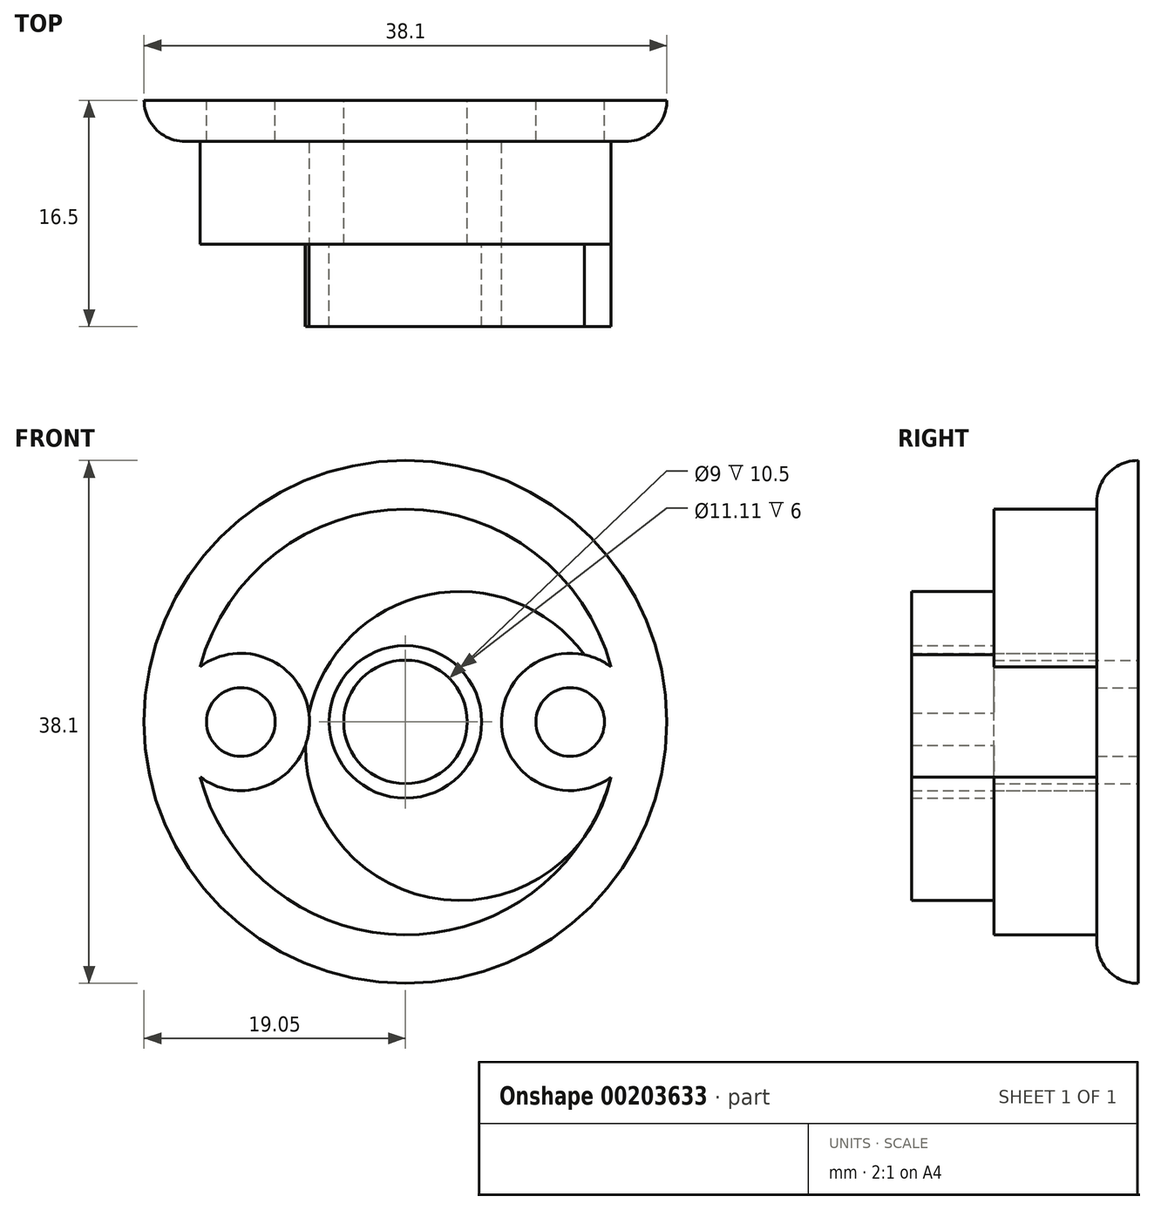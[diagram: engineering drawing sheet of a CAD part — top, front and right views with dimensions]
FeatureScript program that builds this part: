
annotation { "Feature Type Name" : "Feature", "Feature Type Description" : "" }
export const myFeature = defineFeature(function(context is Context, id is Id, definition is map)
    precondition{}
    {
        {
            var Q0;
            Q0=qCreatedBy(makeId("Front.planeOp"),FACE);
            var sketch = newSketch(context, id + "F0", { "sketchPlane" : qUnion([Q0])});
            skCircle(sketch, "E0", {"center": v(0, 0) * mm, "radius": 19.05 * mm});
            skCircle(sketch, "E1", {"center": v(0, 0) * mm, "radius": 4.5 * mm});
            skCircle(sketch, "E2", {"center": v(-12, 0) * mm, "radius": 2.5 * mm});
            skCircle(sketch, "E3.MirrorC", {"center": v(12, 0) * mm, "radius": 2.5 * mm});
            skSolve(sketch);
        }
        {
            var Q0;
            Q0 = qSketchRegion(id + "F0", true);
            extrude(context, id + "F1", {"entities" : qUnion([Q0]), "depth" : 3 * mm});
        }
        {
            var Q0;
            Q0=makeQuery(id+"F1.opExtrude","CAP_EDGE",EDGE,{"disambiguationData":[OSD([sQuery(id+"F0.wireOp",EDGE,"E0")])],"isStart":false});
            fillet(context, id + "F2", {"entities" : qUnion([Q0]), "radius" : 3 * mm, "tangentPropagation" : true, "allowEdgeOverflow" : false});
        }
        {
            var Q0;
            Q0=makeQuery(id+"F1.opExtrude","CAP_FACE",FACE,{"disambiguationData":[OSD([sQuery(id+"F0.wireOp",EDGE,"E0"),sQuery(id+"F0.wireOp",EDGE,"E1"),sQuery(id+"F0.wireOp",EDGE,"E2"),sQuery(id+"F0.wireOp",EDGE,"E3.MirrorC")])],"isStart":false});
            var sketch = newSketch(context, id + "F3", { "sketchPlane" : qUnion([Q0])});
            skCircle(sketch, "E4", {"center": v(0, 0) * mm, "radius": 15.5 * mm});
            skCircle(sketch, "E5.0", {"center": v(0, 0) * mm, "radius": 4.5 * mm});
            skCircle(sketch, "E6", {"center": v(-12, 0) * mm, "radius": 5 * mm});
            skCircle(sketch, "E7.MirrorC", {"center": v(12, 0) * mm, "radius": 5 * mm});
            skSolve(sketch);
        }
        {
            var Q0;
            Q0=makeQuery(id+"F3.imprint","IMPRINT",FACE,{"disambiguationData":[TD([[makeQuery(id+"F3.imprint","IMPRINT",EDGE,{"derivedFrom":sQuery(id+"F3.wireOp",EDGE,"E5.0")}),-1.0]])]});
            extrude(context, id + "F4", {"entities" : qUnion([Q0]), "operationType" : NewBodyOperationType.ADD, "depth" : 7.5 * mm});
        }
        {
            var Q0;
            Q0=makeQuery(id+"F4.opExtrude","CAP_FACE",FACE,{"disambiguationData":[OSD([sQuery(id+"F3.wireOp",EDGE,"E4"),sQuery(id+"F3.wireOp",EDGE,"E5.0"),sQuery(id+"F3.wireOp",EDGE,"E6"),sQuery(id+"F3.wireOp",EDGE,"E7.MirrorC")])],"isStart":false});
            var sketch = newSketch(context, id + "F5", { "sketchPlane" : qUnion([Q0])});
            skCircle(sketch, "E8", {"center": v(0, 0) * mm, "radius": 5.55 * mm});
            skArc(sketch, "E9.0", {"start": v(14.97, -4.02) * mm, "mid": v(7, 0) * mm, "end": v(14.97, 4.02) * mm});
            skCircle(sketch, "E10", {"center": v(3.95, -1.75) * mm, "radius": 11.25 * mm});
            skArc(sketch, "E11.0", {"start": v(-14.97, -4.02) * mm, "mid": v(-7, 0) * mm, "end": v(-14.97, 4.02) * mm});
            skSolve(sketch);
        }
        {
            var Q0;
            {var subQ0=sQuery(id+"F5.wireOp",EDGE,"E10");var subQ1=sQuery(id+"F3.wireOp",EDGE,"E4");var subQ2=makeQuery(id+"F4.opExtrude","CAP_EDGE",EDGE,{"disambiguationData":[OSD([subQ1]),TDD([makeQuery(id+"F3.imprint","IMPRINT",EDGE,{"disambiguationData":[TD([[makeQuery(id+"F3.imprint","INTERSECT",VERTEX,{"disambiguationData":[OD(1.0)],"derivedFrom":[subQ1,sQuery(id+"F3.wireOp",EDGE,"E6")]}),-1.0]])],"derivedFrom":subQ1})])],"isStart":false});var subQ4=makeQuery(id+"F5.imprint","INTERSECT",VERTEX,{"derivedFrom":[subQ2,subQ0]});Q0=makeQuery(id+"F5.imprint","IMPRINT",FACE,{"disambiguationData":[TD([[makeQuery(id+"F5.imprint","IMPRINT",EDGE,{"disambiguationData":[TD([[subQ4,-1.0]])],"derivedFrom":subQ0}),1.0]])]});}
            var Q1;
            Q1=makeQuery(id+"F5.imprint","IMPRINT",FACE,{"disambiguationData":[TD([[makeQuery(id+"F5.imprint","IMPRINT",EDGE,{"derivedFrom":sQuery(id+"F5.wireOp",EDGE,"E8")}),-1.0]])]});
            extrude(context, id + "F6", {"entities" : qUnion([Q0, Q1]), "operationType" : NewBodyOperationType.ADD, "depth" : 6 * mm});
        }
    });
